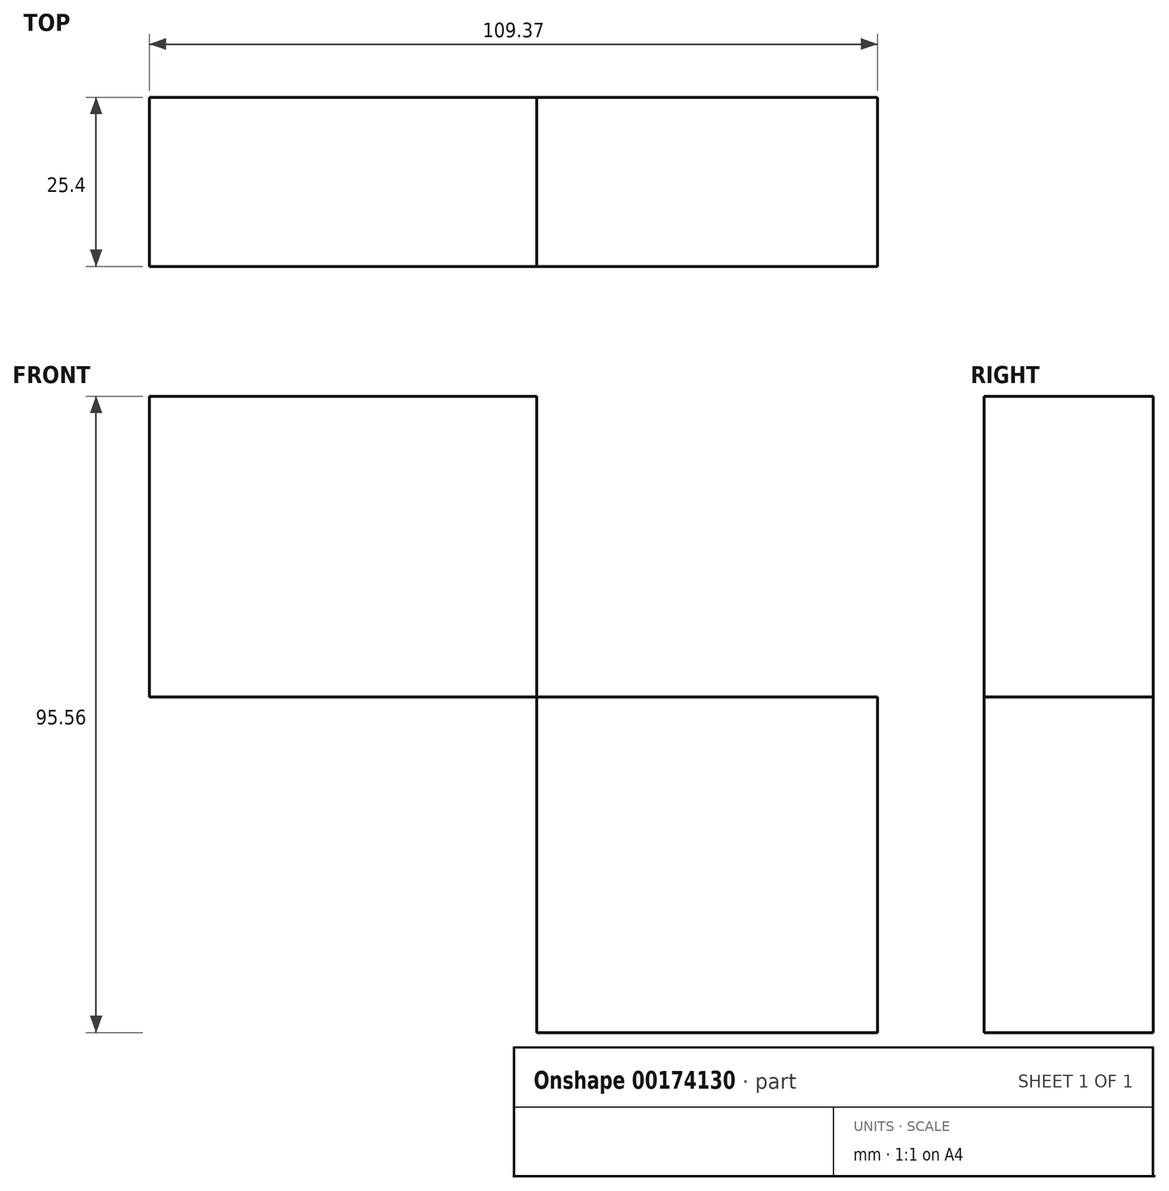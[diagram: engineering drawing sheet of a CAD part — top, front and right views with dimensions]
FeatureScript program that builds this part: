
annotation { "Feature Type Name" : "Feature", "Feature Type Description" : "" }
export const myFeature = defineFeature(function(context is Context, id is Id, definition is map)
    precondition{}
    {
        {
            var Q0;
            Q0=qCreatedBy(makeId("Front.planeOp"),FACE);
            var sketch = newSketch(context, id + "F0", { "sketchPlane" : qUnion([Q0])});
            skCircle(sketch, "E0", {"center": v(0, 0) * mm, "radius": 54.74 * mm});
            skSolve(sketch);
        }
        {
            var Q0;
            Q0=makeQuery(id+"F0.imprint","IMPRINT",FACE,{"disambiguationData":[TD([[makeQuery(id+"F0.imprint","IMPRINT",EDGE,{"derivedFrom":sQuery(id+"F0.wireOp",EDGE,"E0")}),1.0]])]});
            extrude(context, id + "F1", {"entities" : qUnion([Q0]), "depth" : 25.4 * mm});
        }
        {
            var Q0;
            Q0=makeQuery(id+"F1.opExtrude","CAP_FACE",FACE,{"disambiguationData":[OSD([sQuery(id+"F0.wireOp",EDGE,"E0")])],"isStart":false});
            var sketch = newSketch(context, id + "F2", { "sketchPlane" : qUnion([Q0])});
            skCircle(sketch, "E1", {"center": v(0, 0) * mm, "radius": 36.27 * mm});
            skSolve(sketch);
        }
        {
            var Q0;
            Q0=makeQuery(id+"F2.imprint","IMPRINT",FACE,{"disambiguationData":[TD([[makeQuery(id+"F2.imprint","IMPRINT",EDGE,{"derivedFrom":sQuery(id+"F2.wireOp",EDGE,"E1")}),1.0]])]});
            extrude(context, id + "F3", {"entities" : qUnion([Q0]), "operationType" : NewBodyOperationType.ADD, "depth" : 25.4 * mm});
        }
        {
            var Q0;
            Q0=makeQuery(id+"F3.opExtrude","CAP_FACE",FACE,{"disambiguationData":[OSD([sQuery(id+"F2.wireOp",EDGE,"E1")])],"isStart":false});
            var sketch = newSketch(context, id + "F4", { "sketchPlane" : qUnion([Q0])});
            skCircle(sketch, "E2", {"center": v(0, 0) * mm, "radius": 11.12 * mm});
            skSolve(sketch);
        }
        {
            var Q0;
            Q0=makeQuery(id+"F4.imprint","IMPRINT",FACE,{"disambiguationData":[TD([[makeQuery(id+"F4.imprint","IMPRINT",EDGE,{"derivedFrom":sQuery(id+"F4.wireOp",EDGE,"E2")}),1.0]])]});
            extrude(context, id + "F5", {"entities" : qUnion([Q0]), "operationType" : NewBodyOperationType.ADD, "depth" : 25.4 * mm});
        }
        {
            var Q0;
            Q0=makeQuery(id+"F1.opExtrude","CAP_FACE",FACE,{"disambiguationData":[OSD([sQuery(id+"F0.wireOp",EDGE,"E0")])],"isStart":false});
            var Q1;
            Q1 = qSketchRegion(id + "F2", true);
            extrude(context, id + "F6", {"entities" : qUnion([Q0, Q1]), "operationType" : NewBodyOperationType.INTERSECT, "oppositeDirection" : true, "depth" : 25.4 * mm});
        }
        {
            var Q0;
            Q0=makeQuery(id+"F1.opExtrude","SWEPT_BODY",BODY,{"disambiguationData":[OSD([sQuery(id+"F0.wireOp",EDGE,"E0")])]});
            deleteBodies(context, id + "F7", {"entities" : qUnion([Q0])});
        }
        {
            var Q0;
            Q0=qCreatedBy(makeId("Front.planeOp"),FACE);
            var sketch = newSketch(context, id + "F8", { "sketchPlane" : qUnion([Q0])});
            skLineSegment(sketch, "E3.bottom", {"start": v(0, 0) * mm, "end": v(-58.14, 0) * mm});
            skLineSegment(sketch, "E3.top", {"start": v(0, 45.19) * mm, "end": v(-58.14, 45.19) * mm});
            skLineSegment(sketch, "E3.left", {"start": v(0, 0) * mm, "end": v(0, 45.19) * mm});
            skLineSegment(sketch, "E3.right", {"start": v(-58.14, 0) * mm, "end": v(-58.14, 45.19) * mm});
            skLineSegment(sketch, "E4.bottom", {"start": v(0, 0) * mm, "end": v(51.23, 0) * mm});
            skLineSegment(sketch, "E4.top", {"start": v(0, -50.37) * mm, "end": v(51.23, -50.37) * mm});
            skLineSegment(sketch, "E4.left", {"start": v(0, 0) * mm, "end": v(0, -50.37) * mm});
            skLineSegment(sketch, "E4.right", {"start": v(51.23, 0) * mm, "end": v(51.23, -50.37) * mm});
            skSolve(sketch);
        }
        {
            var Q0;
            Q0 = qSketchRegion(id + "F8", true);
            extrude(context, id + "F9", {"entities" : qUnion([Q0]), "depth" : 25.4 * mm});
        }
    });
